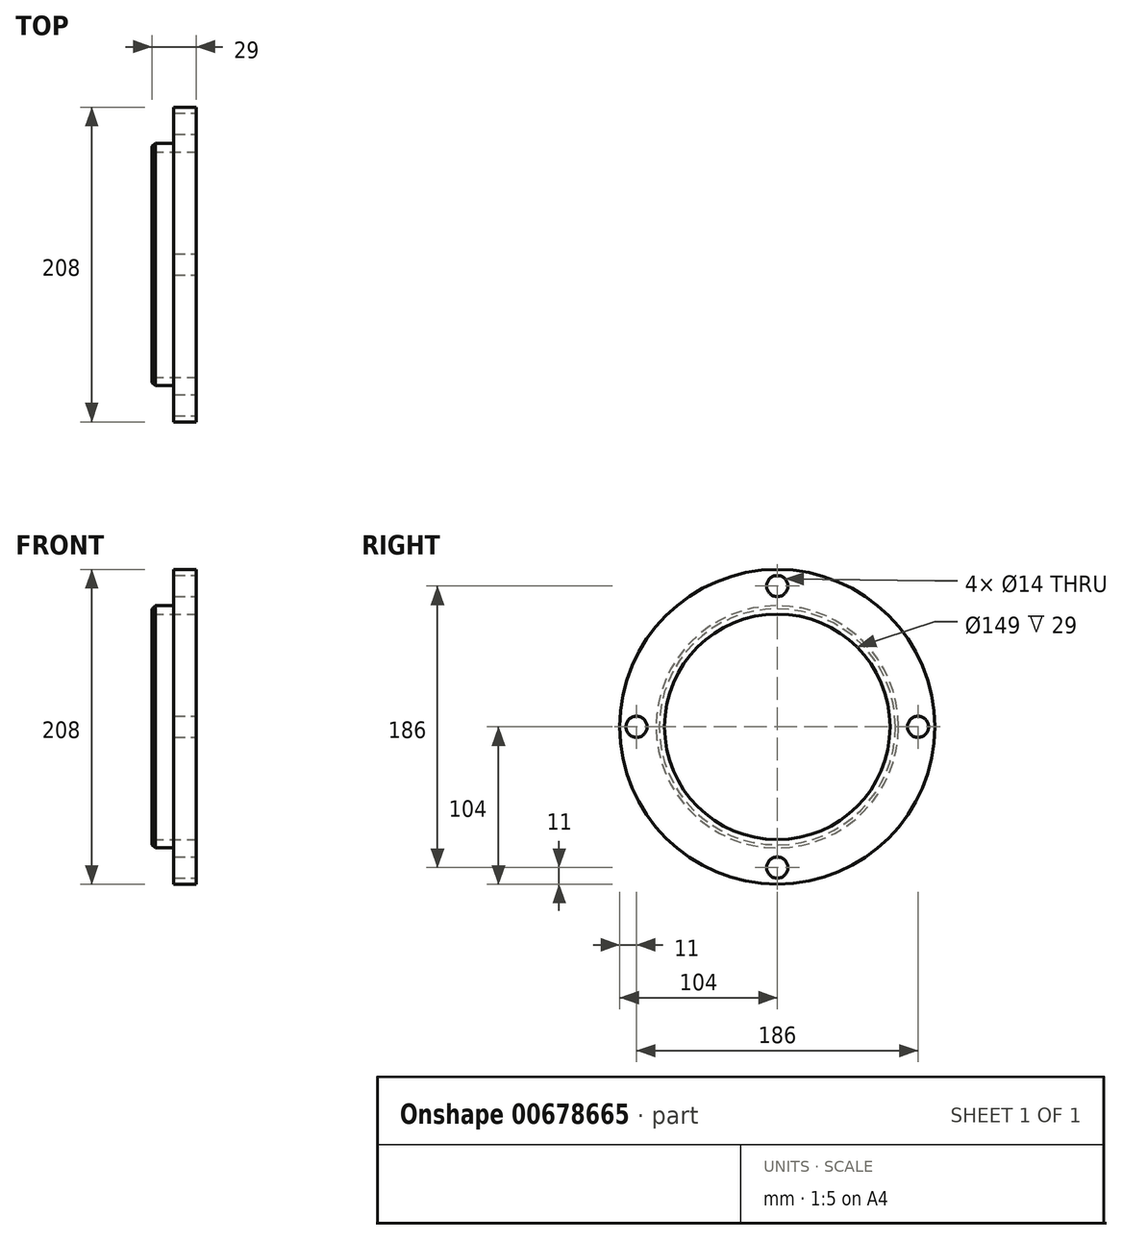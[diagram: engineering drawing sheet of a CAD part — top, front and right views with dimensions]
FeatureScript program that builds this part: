
annotation { "Feature Type Name" : "Feature", "Feature Type Description" : "" }
export const myFeature = defineFeature(function(context is Context, id is Id, definition is map)
    precondition{}
    {
        {
            var Q0;
            Q0=qCreatedBy(makeId("Right.planeOp"),FACE);
            var sketch = newSketch(context, id + "F0", { "sketchPlane" : qUnion([Q0])});
            skCircle(sketch, "E0", {"center": v(0, 0) * mm, "radius": 104 * mm});
            skSolve(sketch);
        }
        {
            var Q0;
            Q0 = qSketchRegion(id + "F0", true);
            extrude(context, id + "F1", {"entities" : qUnion([Q0]), "depth" : (29 - 14.1) * mm, "offsetDistance" : 25 * mm});
        }
        {
            var Q0;
            Q0=makeQuery(id+"F1.opExtrude","CAP_FACE",FACE,{"disambiguationData":[OSD([sQuery(id+"F0.wireOp",EDGE,"E0")])],"isStart":true});
            var sketch = newSketch(context, id + "F2", { "sketchPlane" : qUnion([Q0])});
            skCircle(sketch, "E1", {"center": v(0, 0) * mm, "radius": 80 * mm});
            skSolve(sketch);
        }
        {
            var Q0;
            Q0 = qSketchRegion(id + "F2", true);
            extrude(context, id + "F3", {"entities" : qUnion([Q0]), "operationType" : NewBodyOperationType.ADD, "depth" : 14.1 * mm, "offsetDistance" : 25 * mm});
        }
        {
            var Q0;
            Q0=makeQuery(id+"F3.opExtrude","CAP_EDGE",EDGE,{"disambiguationData":[OSD([sQuery(id+"F2.wireOp",EDGE,"E1")])],"isStart":false});
            chamfer(context, id + "F4", {"entities" : qUnion([Q0]), "width" : 2 * mm, "tangentPropagation" : true});
        }
        {
            var Q0;
            Q0=makeQuery(id+"F1.opExtrude","CAP_FACE",FACE,{"disambiguationData":[OSD([sQuery(id+"F0.wireOp",EDGE,"E0")])],"isStart":false});
            var sketch = newSketch(context, id + "F5", { "sketchPlane" : qUnion([Q0])});
            skPoint(sketch, "E2", {"position": v(0, 0) * mm});
            skSolve(sketch);
        }
        {
            var Q0;
            Q0=sQuery(id+"F5.wireOp",VERTEX,"E2");
            var Q1;
            Q1=makeQuery(id+"F1.opExtrude","SWEPT_BODY",BODY,{"disambiguationData":[OSD([sQuery(id+"F0.wireOp",EDGE,"E0")])]});
            hole(context, id + "F6", {"style" : HoleStyle.SIMPLE, "endStyle" : HoleEndStyle.THROUGH, "holeDiameter" : 149 * mm, "majorDiameter" : 5 * mm, "isTappedThrough" : true, "tappedDepth" : 24.75 * mm, "tapClearance" : 3, "locations" : qUnion([Q0]), "scope" : qUnion([Q1])});
        }
        {
            var Q0;
            Q0=makeQuery(id+"F1.opExtrude","CAP_FACE",FACE,{"disambiguationData":[OSD([sQuery(id+"F0.wireOp",EDGE,"E0")])],"isStart":false});
            var sketch = newSketch(context, id + "F7", { "sketchPlane" : qUnion([Q0])});
            skCircle(sketch, "E3", {"center": v(0, 0) * mm, "radius": 93 * mm, "construction": true});
            skLineSegment(sketch, "E4", {"start": v(0, 0) * mm, "end": v(115.14, 0) * mm, "construction": true});
            skPoint(sketch, "E5", {"position": v(93, 0) * mm});
            skPoint(sketch, "E6.1.0", {"position": v(0, 93) * mm});
            skPoint(sketch, "E6.2.0", {"position": v(-93, 0) * mm});
            skPoint(sketch, "E6.3.0", {"position": v(0, -93) * mm});
            skSolve(sketch);
        }
        {
            var Q0;
            Q0=sQuery(id+"F7.wireOp",VERTEX,"E5");
            var Q1;
            Q1=sQuery(id+"F7.wireOp",VERTEX,"E6.3.0");
            var Q2;
            Q2=sQuery(id+"F7.wireOp",VERTEX,"E6.2.0");
            var Q3;
            Q3=sQuery(id+"F7.wireOp",VERTEX,"E6.1.0");
            var Q4;
            Q4=makeQuery(id+"F1.opExtrude","SWEPT_BODY",BODY,{"disambiguationData":[OSD([sQuery(id+"F0.wireOp",EDGE,"E0")])]});
            hole(context, id + "F8", {"style" : HoleStyle.SIMPLE, "endStyle" : HoleEndStyle.THROUGH, "holeDiameter" : 14 * mm, "majorDiameter" : 5 * mm, "isTappedThrough" : true, "tappedDepth" : 24.75 * mm, "tapClearance" : 3, "locations" : qUnion([Q0, Q1, Q2, Q3]), "scope" : qUnion([Q4])});
        }
    });
